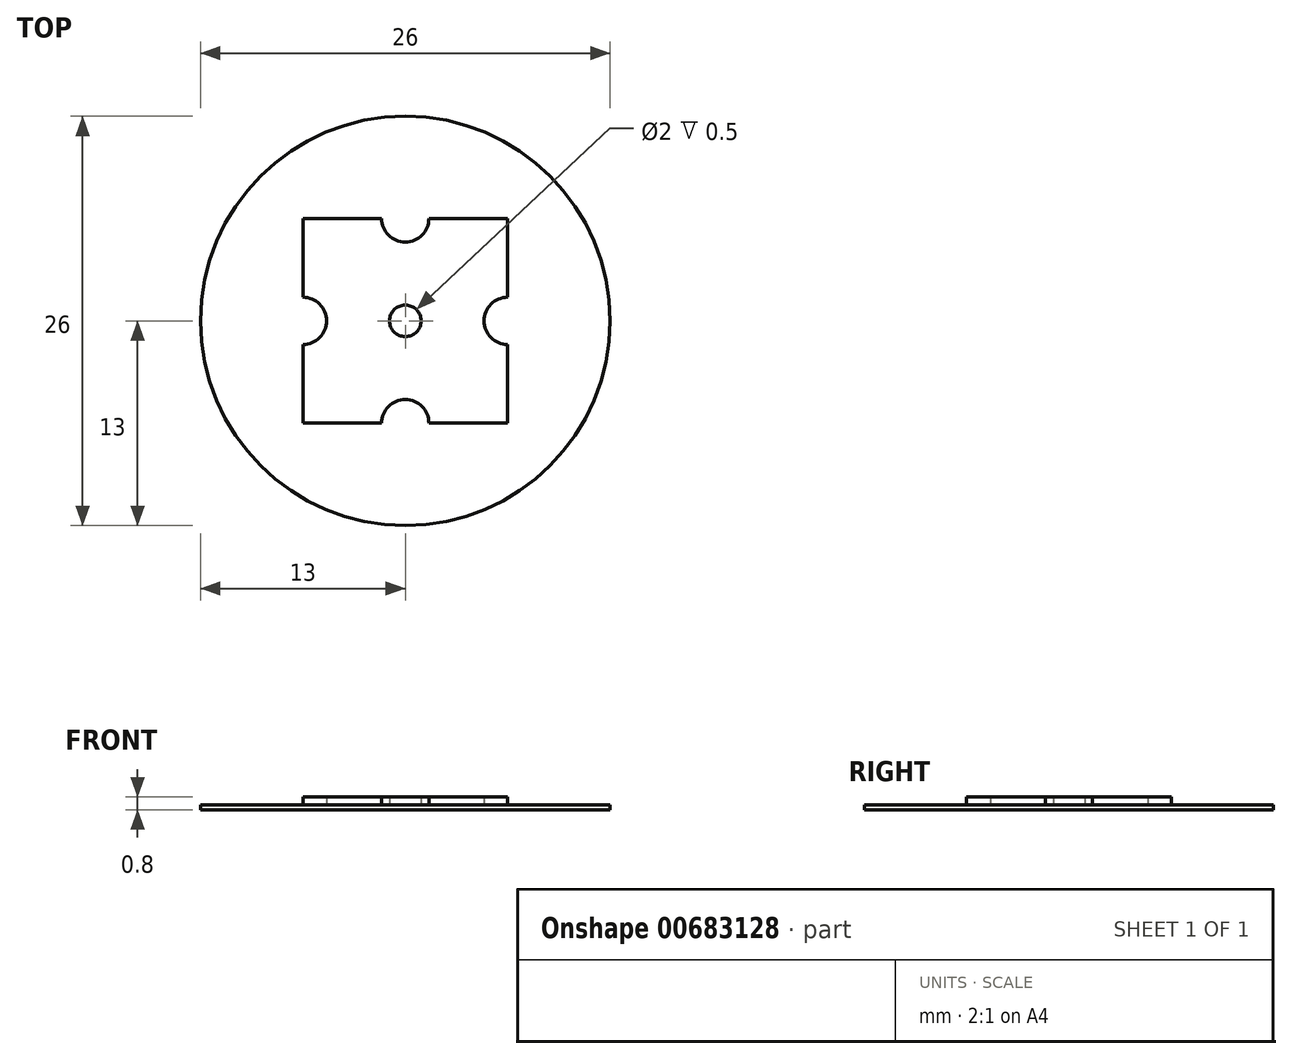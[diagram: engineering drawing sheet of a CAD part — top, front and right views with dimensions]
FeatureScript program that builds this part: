
annotation { "Feature Type Name" : "Feature", "Feature Type Description" : "" }
export const myFeature = defineFeature(function(context is Context, id is Id, definition is map)
    precondition{}
    {
        {
            var Q0;
            Q0=qCreatedBy(makeId("Top.planeOp"),FACE);
            var sketch = newSketch(context, id + "F0", { "sketchPlane" : qUnion([Q0])});
            skCircle(sketch, "E0", {"center": v(0, 0) * mm, "radius": 13 * mm});
            skSolve(sketch);
        }
        {
            var Q0;
            Q0 = qSketchRegion(id + "F0", true);
            extrude(context, id + "F1", {"entities" : qUnion([Q0]), "depth" : .3 * mm, "offsetDistance" : 25 * mm});
        }
        {
            var Q0;
            Q0=makeQuery(id+"F1.opExtrude","CAP_FACE",FACE,{"disambiguationData":[OSD([sQuery(id+"F0.wireOp",EDGE,"E0")])],"isStart":false});
            var sketch = newSketch(context, id + "F2", { "sketchPlane" : qUnion([Q0])});
            skLineSegment(sketch, "E1.bottom", {"start": v(6.5, 6.5) * mm, "end": v(1.5, 6.5) * mm});
            skLineSegment(sketch, "E1.top", {"start": v(6.5, -6.5) * mm, "end": v(1.5, -6.5) * mm});
            skLineSegment(sketch, "E1.left", {"start": v(6.5, 6.5) * mm, "end": v(6.5, 1.5) * mm});
            skLineSegment(sketch, "E1.right", {"start": v(-6.5, 6.5) * mm, "end": v(-6.5, 1.5) * mm});
            skPoint(sketch, "E1.middle", {"position": v(0, 0) * mm});
            skCircle(sketch, "E2", {"center": v(0, 0) * mm, "radius": 1 * mm});
            skArc(sketch, "E3", {"start": v(-1.5, 6.5) * mm, "mid": v(0, 5) * mm, "end": v(1.5, 6.5) * mm});
            skArc(sketch, "E4.1.0", {"start": v(-6.5, -1.5) * mm, "mid": v(-5, 0) * mm, "end": v(-6.5, 1.5) * mm});
            skArc(sketch, "E4.2.0", {"start": v(1.5, -6.5) * mm, "mid": v(0, -5) * mm, "end": v(-1.5, -6.5) * mm});
            skArc(sketch, "E4.3.0", {"start": v(6.5, 1.5) * mm, "mid": v(5, 0) * mm, "end": v(6.5, -1.5) * mm});
            skLineSegment(sketch, "E5.trimOffspring", {"start": v(-1.5, 6.5) * mm, "end": v(-6.5, 6.5) * mm});
            skLineSegment(sketch, "E6.trimOffspring", {"start": v(6.5, -1.5) * mm, "end": v(6.5, -6.5) * mm});
            skLineSegment(sketch, "E7.trimOffspring", {"start": v(-1.5, -6.5) * mm, "end": v(-6.5, -6.5) * mm});
            skLineSegment(sketch, "E8.trimOffspring", {"start": v(-6.5, -1.5) * mm, "end": v(-6.5, -6.5) * mm});
            skSolve(sketch);
        }
        {
            var Q0;
            Q0 = qSketchRegion(id + "F2", true);
            extrude(context, id + "F3", {"entities" : qUnion([Q0]), "operationType" : NewBodyOperationType.ADD, "depth" : .5 * mm, "offsetDistance" : 25 * mm});
        }
    });
